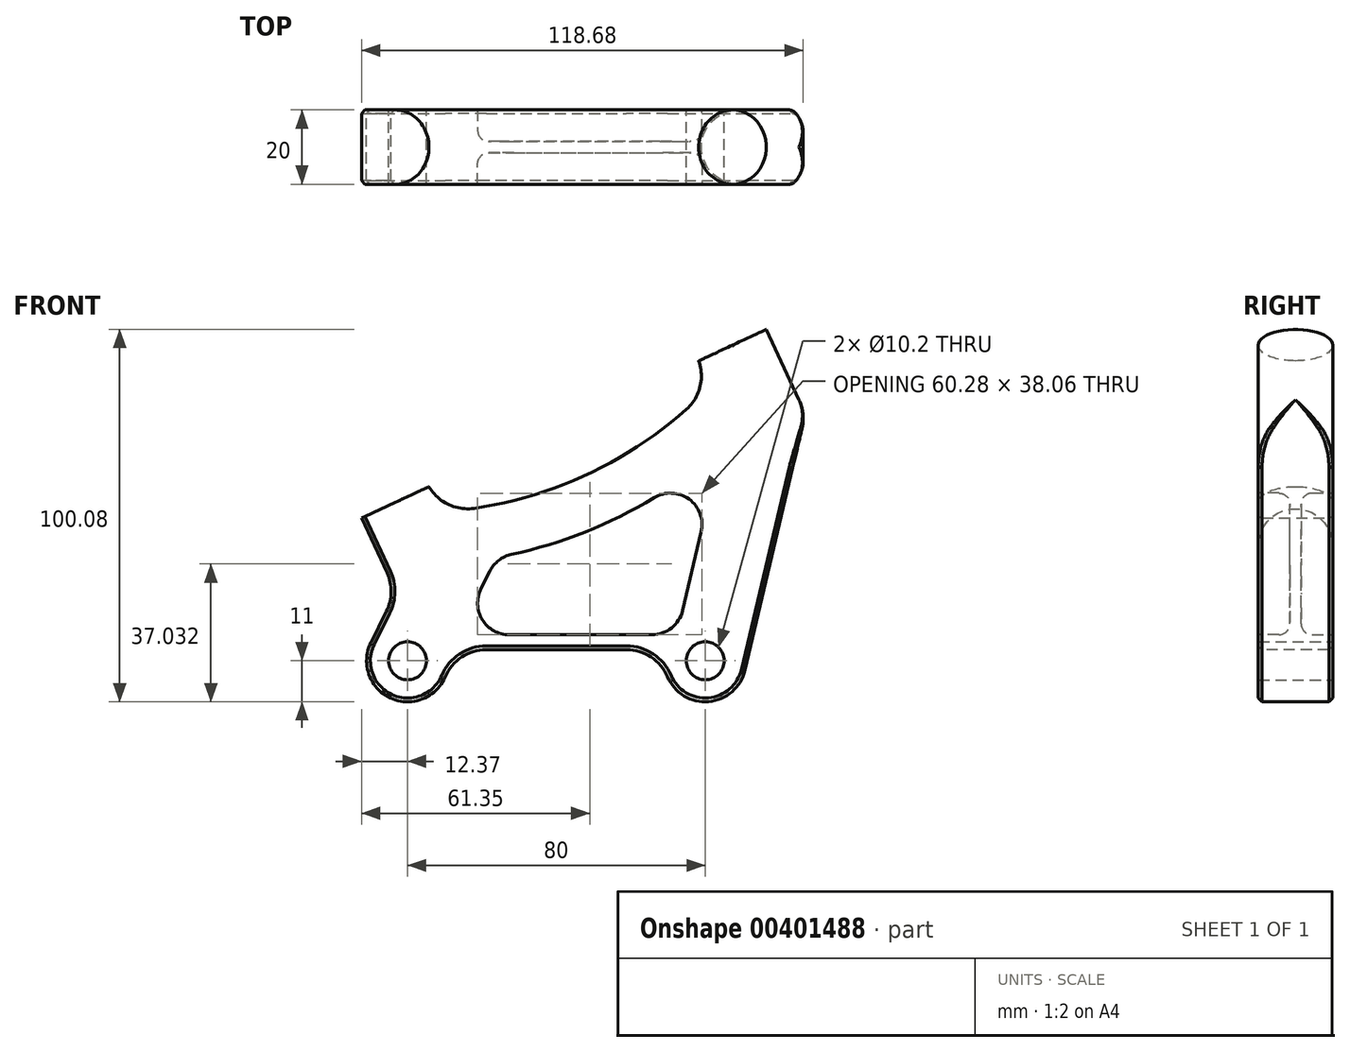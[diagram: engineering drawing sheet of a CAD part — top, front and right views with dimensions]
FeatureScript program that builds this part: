
annotation { "Feature Type Name" : "Feature", "Feature Type Description" : "" }
export const myFeature = defineFeature(function(context is Context, id is Id, definition is map)
    precondition{}
    {
        {
            var Q0;
            Q0=qCreatedBy(makeId("Front.planeOp"),FACE);
            var sketch = newSketch(context, id + "F0", { "sketchPlane" : qUnion([Q0])});
            skCircle(sketch, "E0", {"center": v(0, 0) * mm, "radius": 5.1 * mm});
            skCircle(sketch, "E1", {"center": v(80, 0) * mm, "radius": 5.1 * mm});
            skCircle(sketch, "E2", {"center": v(0, 0) * mm, "radius": 11 * mm});
            skCircle(sketch, "E3", {"center": v(80, 0) * mm, "radius": 11 * mm});
            skLineSegment(sketch, "E4", {"start": v(10.58, 3) * mm, "end": v(69.42, 3) * mm});
            skLineSegment(sketch, "E5", {"start": v(-5.53, 23.68) * mm, "end": v(-12.37, 38.37) * mm});
            skLineSegment(sketch, "E6", {"start": v(-12.37, 38.37) * mm, "end": v(5.75, 46.82) * mm});
            skLineSegment(sketch, "E7", {"start": v(96.38, 89.08) * mm, "end": v(105.2, 70.2) * mm});
            skLineSegment(sketch, "E8", {"start": v(-5.67, 13.24) * mm, "end": v(-9.84, 4.92) * mm});
            skPoint(sketch, "E9.visualSharp", {"position": v(-3.08, 18.43) * mm});
            skArc(sketch, "E9.filletArc", {"start": v(-5.67, 13.24) * mm, "mid": v(-4.4, 18.45) * mm, "end": v(-5.53, 23.68) * mm});
            skLineSegment(sketch, "E10", {"start": v(106, 62.37) * mm, "end": v(90.7, -2.52) * mm});
            skLineSegment(sketch, "E11", {"start": v(42, 63.72) * mm, "end": v(1.86, 149.82) * mm, "construction": true});
            skLineSegment(sketch, "E12", {"start": v(5.75, 46.82) * mm, "end": v(8.9, 40.05) * mm});
            skLineSegment(sketch, "E13", {"start": v(78.26, 80.63) * mm, "end": v(81.41, 73.86) * mm});
            skLineSegment(sketch, "E14.trimOffspring", {"start": v(78.26, 80.63) * mm, "end": v(96.38, 89.08) * mm});
            skArc(sketch, "E15", {"start": v(8.9, 40.05) * mm, "mid": v(48.34, 50.13) * mm, "end": v(81.41, 73.86) * mm});
            skPoint(sketch, "E16.visualSharp", {"position": v(106.95, 66.42) * mm});
            skArc(sketch, "E16.filletArc", {"start": v(106, 62.37) * mm, "mid": v(106.25, 66.35) * mm, "end": v(105.2, 70.2) * mm});
            skSolve(sketch);
        }
        {
            var Q0;
            {var subQ2=sQuery(id+"F0.wireOp",EDGE,"E4");Q0=makeQuery(id+"F0.imprint","IMPRINT",FACE,{"disambiguationData":[TD([[makeQuery(id+"F0.imprint","IMPRINT",EDGE,{"derivedFrom":subQ2}),1.0]])]});}
            var Q1;
            Q1=makeQuery(id+"F0.imprint","IMPRINT",FACE,{"disambiguationData":[TD([[makeQuery(id+"F0.imprint","IMPRINT",EDGE,{"derivedFrom":sQuery(id+"F0.wireOp",EDGE,"E0")}),-1.0]])]});
            var Q2;
            Q2=makeQuery(id+"F0.imprint","IMPRINT",FACE,{"disambiguationData":[TD([[makeQuery(id+"F0.imprint","IMPRINT",EDGE,{"derivedFrom":sQuery(id+"F0.wireOp",EDGE,"E1")}),-1.0]])]});
            extrude(context, id + "F1", {"entities" : qUnion([Q0, Q1, Q2]), "depth" : 20 * mm});
        }
        {
            var Q0;
            Q0=makeQuery(id+"F1.opExtrude","CAP_FACE",FACE,{"disambiguationData":[OSD([sQuery(id+"F0.wireOp",EDGE,"E0"),sQuery(id+"F0.wireOp",EDGE,"E1"),sQuery(id+"F0.wireOp",EDGE,"E2"),sQuery(id+"F0.wireOp",EDGE,"E3"),sQuery(id+"F0.wireOp",EDGE,"E4"),sQuery(id+"F0.wireOp",EDGE,"E5"),sQuery(id+"F0.wireOp",EDGE,"E6"),sQuery(id+"F0.wireOp",EDGE,"E7"),sQuery(id+"F0.wireOp",EDGE,"E8"),sQuery(id+"F0.wireOp",EDGE,"E9.filletArc"),sQuery(id+"F0.wireOp",EDGE,"E10"),sQuery(id+"F0.wireOp",EDGE,"E12"),sQuery(id+"F0.wireOp",EDGE,"E13"),sQuery(id+"F0.wireOp",EDGE,"E14.trimOffspring"),sQuery(id+"F0.wireOp",EDGE,"E15"),sQuery(id+"F0.wireOp",EDGE,"E16.filletArc")])],"isStart":false});
            var sketch = newSketch(context, id + "F2", { "sketchPlane" : qUnion([Q0])});
            skLineSegment(sketch, "E17", {"start": v(24, 27.81) * mm, "end": v(13.57, 7) * mm});
            skLineSegment(sketch, "E18", {"start": v(13.57, 7) * mm, "end": v(72.4, 7) * mm});
            skLineSegment(sketch, "E19", {"start": v(72.4, 7) * mm, "end": v(84.2, 57.12) * mm});
            skArc(sketch, "E20", {"start": v(24, 27.81) * mm, "mid": v(56.12, 38.32) * mm, "end": v(84.2, 57.12) * mm});
            skSolve(sketch);
        }
        {
            var Q0;
            Q0=makeQuery(id+"F1.opExtrude","CAP_FACE",FACE,{"disambiguationData":[OSD([sQuery(id+"F0.wireOp",EDGE,"E0"),sQuery(id+"F0.wireOp",EDGE,"E1"),sQuery(id+"F0.wireOp",EDGE,"E2"),sQuery(id+"F0.wireOp",EDGE,"E3"),sQuery(id+"F0.wireOp",EDGE,"E4"),sQuery(id+"F0.wireOp",EDGE,"E5"),sQuery(id+"F0.wireOp",EDGE,"E6"),sQuery(id+"F0.wireOp",EDGE,"E7"),sQuery(id+"F0.wireOp",EDGE,"E8"),sQuery(id+"F0.wireOp",EDGE,"E9.filletArc"),sQuery(id+"F0.wireOp",EDGE,"E10"),sQuery(id+"F0.wireOp",EDGE,"E12"),sQuery(id+"F0.wireOp",EDGE,"E13"),sQuery(id+"F0.wireOp",EDGE,"E14.trimOffspring"),sQuery(id+"F0.wireOp",EDGE,"E15"),sQuery(id+"F0.wireOp",EDGE,"E16.filletArc")])],"isStart":true});
            var sketch = newSketch(context, id + "F3", { "sketchPlane" : qUnion([Q0])});
            skLineSegment(sketch, "E21.0", {"start": v(-72.4, 7) * mm, "end": v(-84.2, 57.12) * mm});
            skArc(sketch, "E22.0", {"start": v(-24, 27.81) * mm, "mid": v(-56.12, 38.32) * mm, "end": v(-84.2, 57.12) * mm});
            skLineSegment(sketch, "E23.0", {"start": v(-24, 27.81) * mm, "end": v(-13.57, 7) * mm});
            skLineSegment(sketch, "E24.0", {"start": v(-13.57, 7) * mm, "end": v(-72.4, 7) * mm});
            skSolve(sketch);
        }
        {
            var Q0;
            Q0=makeQuery(id+"F2.imprint","IMPRINT",FACE,{"disambiguationData":[TD([[makeQuery(id+"F2.imprint","IMPRINT",EDGE,{"derivedFrom":sQuery(id+"F2.wireOp",EDGE,"E17")}),1.0]])]});
            extrude(context, id + "F4", {"entities" : qUnion([Q0]), "operationType" : NewBodyOperationType.REMOVE, "oppositeDirection" : true, "depth" : 8.5 * mm});
        }
        {
            var Q0;
            Q0 = qSketchRegion(id + "F3", true);
            extrude(context, id + "F5", {"entities" : qUnion([Q0]), "operationType" : NewBodyOperationType.REMOVE, "oppositeDirection" : true, "depth" : 8.5 * mm});
        }
        {
            var Q0;
            Q0=makeQuery(id+"F1.opExtrude","SWEPT_EDGE",EDGE,{"disambiguationData":[OSD([sQuery(id+"F0.wireOp",EDGE,"E2"),sQuery(id+"F0.wireOp",EDGE,"E4")])]});
            var Q1;
            Q1=makeQuery(id+"F1.opExtrude","SWEPT_EDGE",EDGE,{"disambiguationData":[OSD([sQuery(id+"F0.wireOp",EDGE,"E12"),sQuery(id+"F0.wireOp",EDGE,"E15")])]});
            var Q2;
            Q2=makeQuery(id+"F1.opExtrude","SWEPT_EDGE",EDGE,{"disambiguationData":[OSD([sQuery(id+"F0.wireOp",EDGE,"E3"),sQuery(id+"F0.wireOp",EDGE,"E4")])]});
            var Q3;
            Q3=makeQuery(id+"F1.opExtrude","SWEPT_EDGE",EDGE,{"disambiguationData":[OSD([sQuery(id+"F0.wireOp",EDGE,"E13"),sQuery(id+"F0.wireOp",EDGE,"E15")])]});
            fillet(context, id + "F6", {"entities" : qUnion([Q0, Q1, Q2, Q3]), "radius" : 12 * mm, "tangentPropagation" : true, "allowEdgeOverflow" : false});
        }
        {
            var Q0;
            Q0=makeQuery(id+"F1.opExtrude","CAP_EDGE",EDGE,{"disambiguationData":[OSD([sQuery(id+"F0.wireOp",EDGE,"E15")])],"isStart":false});
            var Q1;
            Q1=makeQuery(id+"F1.opExtrude","CAP_EDGE",EDGE,{"disambiguationData":[OSD([sQuery(id+"F0.wireOp",EDGE,"E15")])],"isStart":true});
            fillet(context, id + "F7", {"entities" : qUnion([Q0, Q1]), "radius" : 10 * mm, "tangentPropagation" : true, "allowEdgeOverflow" : false});
        }
        {
            var Q0;
            Q0=makeQuery(id+"F1.opExtrude","CAP_EDGE",EDGE,{"disambiguationData":[OSD([sQuery(id+"F0.wireOp",EDGE,"E7")])],"isStart":false});
            var Q1;
            Q1=makeQuery(id+"F1.opExtrude","CAP_EDGE",EDGE,{"disambiguationData":[OSD([sQuery(id+"F0.wireOp",EDGE,"E7")])],"isStart":true});
            fillet(context, id + "F8", {"entities" : qUnion([Q0, Q1]), "radius" : 10 * mm, "allowEdgeOverflow" : false});
        }
        {
            var Q0;
            Q0=makeQuery(id+"F1.opExtrude","CAP_EDGE",EDGE,{"disambiguationData":[OSD([sQuery(id+"F0.wireOp",EDGE,"E4")])],"isStart":false});
            var Q1;
            Q1=makeQuery(id+"F1.opExtrude","CAP_EDGE",EDGE,{"disambiguationData":[OSD([sQuery(id+"F0.wireOp",EDGE,"E8")])],"isStart":true});
            chamfer(context, id + "F9", {"entities" : qUnion([Q0, Q1]), "width" : 1 * mm, "tangentPropagation" : true});
        }
        {
            var Q0;
            Q0=makeQuery(id+"F4.boolean.opBoolean","COPY",EDGE,{"derivedFrom":makeQuery(id+"F4.opExtrude","SWEPT_EDGE",EDGE,{"disambiguationData":[OSD([sQuery(id+"F2.wireOp",EDGE,"dcb88ec1-9035-48cf-81b1-616112557554.0"),sQuery(id+"F2.wireOp",EDGE,"E17")])]})});
            var Q1;
            Q1=makeQuery(id+"F4.boolean.opBoolean","COPY",EDGE,{"derivedFrom":makeQuery(id+"F4.opExtrude","SWEPT_EDGE",EDGE,{"disambiguationData":[OSD([sQuery(id+"F2.wireOp",EDGE,"dcb88ec1-9035-48cf-81b1-616112557554.0"),sQuery(id+"F2.wireOp",EDGE,"E19")])]})});
            var Q2;
            Q2=makeQuery(id+"F4.boolean.opBoolean","COPY",EDGE,{"derivedFrom":makeQuery(id+"F4.opExtrude","SWEPT_EDGE",EDGE,{"disambiguationData":[OSD([sQuery(id+"F2.wireOp",EDGE,"E18"),sQuery(id+"F2.wireOp",EDGE,"E19")])]})});
            var Q3;
            Q3=makeQuery(id+"F4.boolean.opBoolean","COPY",EDGE,{"derivedFrom":makeQuery(id+"F4.opExtrude","SWEPT_EDGE",EDGE,{"disambiguationData":[OSD([sQuery(id+"F2.wireOp",EDGE,"E17"),sQuery(id+"F2.wireOp",EDGE,"E18")])]})});
            var Q4;
            Q4=makeQuery(id+"F5.boolean.opBoolean","COPY",EDGE,{"derivedFrom":makeQuery(id+"F5.opExtrude","SWEPT_EDGE",EDGE,{"disambiguationData":[OSD([sQuery(id+"F3.wireOp",EDGE,"E22.0"),sQuery(id+"F3.wireOp",EDGE,"E23.0")])]})});
            var Q5;
            Q5=makeQuery(id+"F5.boolean.opBoolean","COPY",EDGE,{"derivedFrom":makeQuery(id+"F5.opExtrude","SWEPT_EDGE",EDGE,{"disambiguationData":[OSD([sQuery(id+"F3.wireOp",EDGE,"E21.0"),sQuery(id+"F3.wireOp",EDGE,"E22.0")])]})});
            var Q6;
            Q6=makeQuery(id+"F5.boolean.opBoolean","COPY",EDGE,{"derivedFrom":makeQuery(id+"F5.opExtrude","SWEPT_EDGE",EDGE,{"disambiguationData":[OSD([sQuery(id+"F3.wireOp",EDGE,"E21.0"),sQuery(id+"F3.wireOp",EDGE,"E24.0")])]})});
            var Q7;
            Q7=makeQuery(id+"F5.boolean.opBoolean","COPY",EDGE,{"derivedFrom":makeQuery(id+"F5.opExtrude","SWEPT_EDGE",EDGE,{"disambiguationData":[OSD([sQuery(id+"F3.wireOp",EDGE,"E23.0"),sQuery(id+"F3.wireOp",EDGE,"E24.0")])]})});
            fillet(context, id + "F10", {"entities" : qUnion([Q0, Q1, Q2, Q3, Q4, Q5, Q6, Q7]), "radius" : 8.5 * mm, "tangentPropagation" : true, "allowEdgeOverflow" : false});
        }
        {
            var Q0;
            Q0=makeQuery(id+"F4.boolean.opBoolean","COPY",FACE,{"derivedFrom":makeQuery(id+"F4.opExtrude","CAP_FACE",FACE,{"disambiguationData":[OSD([sQuery(id+"F2.wireOp",EDGE,"dcb88ec1-9035-48cf-81b1-616112557554.0"),sQuery(id+"F2.wireOp",EDGE,"E17"),sQuery(id+"F2.wireOp",EDGE,"E18"),sQuery(id+"F2.wireOp",EDGE,"E19")])],"isStart":false})});
            var Q1;
            Q1=makeQuery(id+"F5.boolean.opBoolean","COPY",EDGE,{"derivedFrom":makeQuery(id+"F5.opExtrude","CAP_EDGE",EDGE,{"disambiguationData":[OSD([sQuery(id+"F3.wireOp",EDGE,"E24.0")])],"isStart":false})});
            fillet(context, id + "F11", {"entities" : qUnion([Q0, Q1]), "radius" : 3 * mm, "tangentPropagation" : true, "allowEdgeOverflow" : false});
        }
        {
            var Q0;
            Q0=makeQuery(id+"F1.opExtrude","SWEPT_FACE",FACE,{"disambiguationData":[OSD([sQuery(id+"F0.wireOp",EDGE,"E6")])]});
            var sketch = newSketch(context, id + "F12", { "sketchPlane" : qUnion([Q0])});
            skLineSegment(sketch, "E25.0", {"start": v(5, -19) * mm, "end": v(5, -1) * mm});
            skLineSegment(sketch, "E26.0.0", {"start": v(5, -1) * mm, "end": v(5, -19) * mm});
            skLineSegment(sketch, "E26.0.1", {"start": v(5, -19) * mm, "end": v(6, -20) * mm});
            skLineSegment(sketch, "E26.0.2", {"start": v(6, -20) * mm, "end": v(14.98, -20) * mm});
            skFitSpline(sketch, "E26.0.3", {"points": [v(14.98, -20) * mm, v(15.64, -20) * mm, v(16.61, -19.9) * mm, v(17.88, -19.59) * mm, v(18.82, -19.25) * mm, v(19.7, -18.84) * mm, v(20.4, -18.42) * mm, v(20.94, -18.04) * mm, v(21.46, -17.64) * mm, v(22.07, -17.09) * mm, v(22.73, -16.36) * mm, v(23.31, -15.58) * mm, v(23.83, -14.73) * mm, v(24.25, -13.84) * mm, v(24.58, -12.92) * mm, v(24.82, -11.96) * mm, v(24.97, -10.99) * mm, v(25, -10.33) * mm, v(25, -10) * mm]});
            skFitSpline(sketch, "E26.0.4", {"points": [v(25, -10) * mm, v(25, -9.34) * mm, v(24.9, -8.36) * mm, v(24.58, -7.1) * mm, v(24.14, -5.85) * mm, v(23.6, -4.85) * mm, v(23.03, -4.04) * mm, v(22.62, -3.52) * mm, v(22.07, -2.92) * mm, v(21.35, -2.26) * mm, v(20.56, -1.68) * mm, v(19.7, -1.17) * mm, v(18.82, -0.75) * mm, v(17.9, -0.42) * mm, v(16.94, -0.18) * mm, v(15.96, -0.03) * mm, v(15.3, 0) * mm, v(14.98, 0) * mm]});
            skLineSegment(sketch, "E26.0.5", {"start": v(14.98, 0) * mm, "end": v(6, 0) * mm});
            skLineSegment(sketch, "E26.0.6", {"start": v(6, 0) * mm, "end": v(5, -1) * mm});
            skArc(sketch, "E27.0.0", {"start": v(115.01, -20) * mm, "mid": v(125, -10) * mm, "end": v(115.01, 0) * mm});
            skFitSpline(sketch, "E27.0.1", {"points": [v(115.02, 0) * mm, v(114.36, 0) * mm, v(113.39, -0.1) * mm, v(112.12, -0.41) * mm, v(111.18, -0.75) * mm, v(110.3, -1.16) * mm, v(109.6, -1.58) * mm, v(109.06, -1.96) * mm, v(108.54, -2.36) * mm, v(107.93, -2.91) * mm, v(107.27, -3.64) * mm, v(106.69, -4.42) * mm, v(106.17, -5.27) * mm, v(105.75, -6.16) * mm, v(105.42, -7.08) * mm, v(105.18, -8.04) * mm, v(105.03, -9.01) * mm, v(105, -9.67) * mm, v(105, -10) * mm]});
            skFitSpline(sketch, "E27.0.2", {"points": [v(105, -10) * mm, v(105, -10.66) * mm, v(105.1, -11.64) * mm, v(105.42, -12.9) * mm, v(105.86, -14.15) * mm, v(106.4, -15.15) * mm, v(106.97, -15.96) * mm, v(107.38, -16.48) * mm, v(107.93, -17.08) * mm, v(108.65, -17.74) * mm, v(109.44, -18.32) * mm, v(110.3, -18.83) * mm, v(111.18, -19.25) * mm, v(112.1, -19.58) * mm, v(113.06, -19.82) * mm, v(114.04, -19.97) * mm, v(114.7, -20) * mm, v(115.02, -20) * mm]});
            skSolve(sketch);
        }
    });
